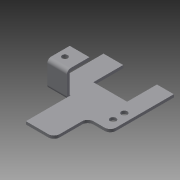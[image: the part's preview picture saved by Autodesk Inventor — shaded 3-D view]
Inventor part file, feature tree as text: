
AUTODESK INVENTOR PART (.ipt)
format: ipt  version: 2013 (Build 170138000, 138)  size: 297,984 bytes
history: native  units: in
note: dims shown in document units (in); Inventor stores cm internally (conversion verified against a paired STEP export)
features: sketch x18, sheet_metal_op x12, other x10, extrude x9, reference x6, chamfer x1
ambient origin geometry x8: Origin, YZ Plane, XZ Plane, XY Plane, X Axis, Y Axis, Z Axis, Center Point
bodies: Solid1 (feature_tree)
feature tree (56):
  sheet_metal_op  "Face1"
  sheet_metal_op  "Flange1"
  extrude  "Extrusion1"  Depth=0.125in
  sketch  "Sketch7"  dims[d10=0.125in d11=2.0in d12=0.0in]
  sketch  "Sketch8"  dims[d19=1.3125in d20=2.1in]
  sketch  "Sketch9"  dims[d21=0.25in d22=0.125in]
  extrude  "Extrusion4"  Depth=0.25in
  extrude  "Extrusion5"  Depth=1.0in TaperAngle=90.0deg
  extrude  "Extrusion6"  Depth=0.125in
  extrude  "Extrusion7"  Depth=2.0in TaperAngle=0.0deg
  sheet_metal_op  "Flange2"
  sheet_metal_op  "Flange3"
  extrude  "Extrusion8"  Depth=2.1in
  extrude  "Extrusion9"  Depth=0.125in
  sheet_metal_op  "Face2"
  chamfer  "Corner Round1"
  extrude  "Extrusion10"  Depth=0.125in TaperAngle=0.0deg
  extrude  "Extrusion11"  Depth=0.125in TaperAngle=0.0deg
  sketch  "Sketch1"  dims[d0=0.125in d1=0.125in]
  other  "Plate1"
  sketch  "Sketch2"  dims[d2=0.0625in d3=0.25in]
  other  "Plate2"
  sheet_metal_op  "Bend1"
  sheet_metal_op  "Corner1"
  sketch  "Sketch3"  dims[d4=0.125in d5=1.0in d6=90.0deg d7=0.05in]
  sketch  "Sketch6"  dims[d8=0.5in d9=0.125in]
  reference  "Reference1"
  sketch  "Sketch10"  dims[d23=0.0in d24=0.125in d25=0.0in]
  sketch  "Sketch11"  dims[d26=0.125in d27=0.0in d28=0.125in d29=0.0in]
  other  "Plate3"
  sheet_metal_op  "Bend2"
  sheet_metal_op  "Corner2"
  sketch  "Sketch12"  dims[d30=0.5in d31=0.0in]
  other  "Plate4"
  sheet_metal_op  "Bend3"
  sheet_metal_op  "Corner3"
  sketch  "Sketch15"  dims[d32=0.125in]
  sketch  "Sketch16"  dims[d33=0.0625in]
  sketch  "Sketch17"  dims[d34=0.25in]
  reference  "Reference2"
  reference  "Reference3"
  reference  "Reference4"
  other  "Plate6"
  sheet_metal_op  "Bend5"
  sketch  "Sketch18"  dims[d35=0.125in]
  sketch  "Sketch19"  dims[d36=1.0in d37=90.0deg d38=0.05in]
  reference  "Reference5"
  reference  "Reference6"
  sketch  "Sketch20"  dims[d39=0.5in]
  sketch  "Sketch22"  dims[d40=0.125in]
  sketch  "Sketch23"  dims[d41=0.125in d42=0.125in d43=0.0625in d44=0.25in d45=0.125in d46=1.0in d47=90.0deg d48=0.05in d49=0.5in d50=0.125in d51=0.125in d64=1.0in d65=2.0in d66=0.0in d67=2.0in d68=0.0in d69=0.125in d70=0.125in d71=0.0625in d72=0.25in d73=0.125in d74=0.75in d75=0.125in d76=0.0in d77=0.125in d78=0.0in d79=0.25in d83=1.5in d84=0.0in d85=0.125in d86=0.0in d87=1.5in d88=0.0in]
  other  "Cut1"
  other  "Cut3"
  other  "Cut4"
  other  "Cut5"
  other  "Definition1"
